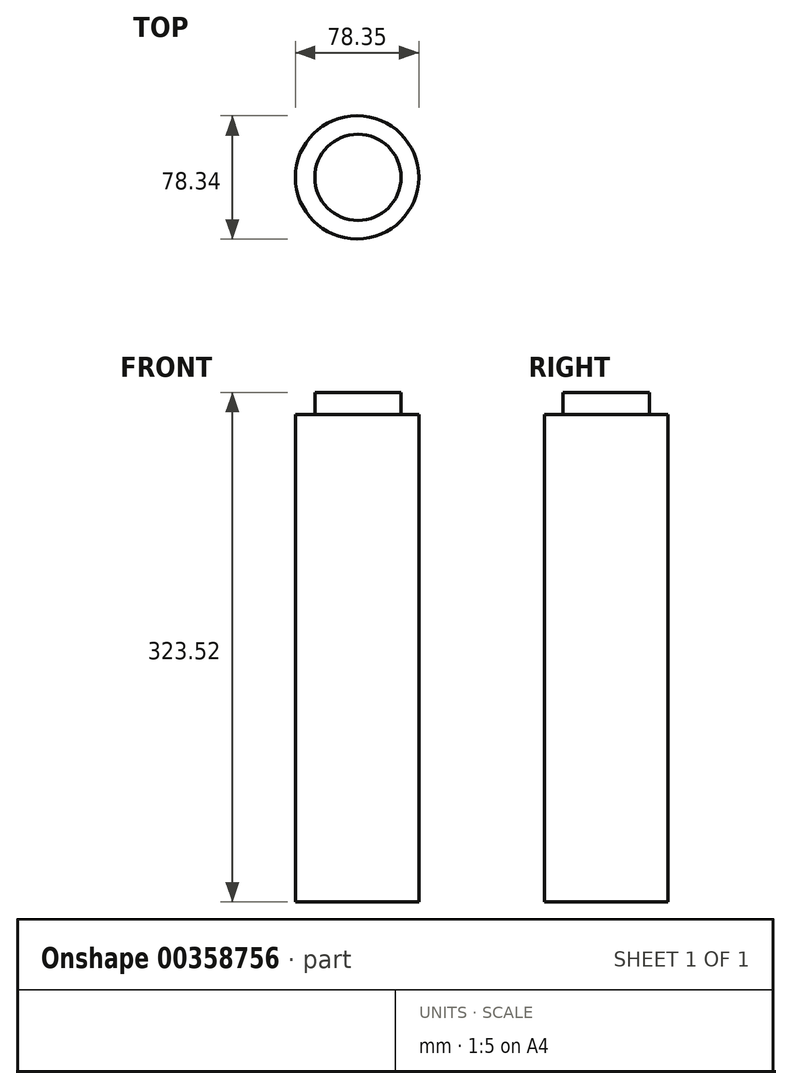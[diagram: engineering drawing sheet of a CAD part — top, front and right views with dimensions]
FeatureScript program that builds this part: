
annotation { "Feature Type Name" : "Feature", "Feature Type Description" : "" }
export const myFeature = defineFeature(function(context is Context, id is Id, definition is map)
    precondition{}
    {
        {
            var Q0;
            Q0=qCreatedBy(makeId("Top.planeOp"),FACE);
            var sketch = newSketch(context, id + "F0", { "sketchPlane" : qUnion([Q0])});
            skCircle(sketch, "E0", {"center": v(-1.87, 0) * mm, "radius": 39.17 * mm});
            skSolve(sketch);
        }
        {
            var Q0;
            Q0 = qSketchRegion(id + "F0", true);
            extrude(context, id + "F1", {"entities" : qUnion([Q0]), "depth" : 309.5 * mm});
        }
        {
            var Q0;
            Q0=makeQuery(id+"F1.opExtrude","SWEPT_BODY",BODY,{"disambiguationData":[OSD([sQuery(id+"F0.wireOp",EDGE,"E0")])]});
            transform(context, id + "F2", {"entities" : qUnion([Q0]), "transformType" : TransformType.TRANSLATION_3D, "dx" : 0 * mm, "dy" : 0 * mm, "dz" : 25 * mm, "makeCopy" : true});
        }
        {
            var Q0;
            Q0=makeQuery(id+"F2.opPattern","COPY",BODY,{"derivedFrom":makeQuery(id+"F1.opExtrude","SWEPT_BODY",BODY,{"disambiguationData":[OSD([sQuery(id+"F0.wireOp",EDGE,"E0")])]}),"instanceName":"1"});
            var Q1;
            Q1=sQuery(id+"F0.wireOp",VERTEX,"E0.center");
            transform(context, id + "F3", {"entities" : qUnion([Q0]), "transformType" : TransformType.SCALE_UNIFORMLY, "scale" : .7, "scalePoint" : qUnion([Q1]), "makeCopy" : false});
        }
        {
            var Q0;
            Q0=makeQuery(id+"F2.opPattern","COPY",BODY,{"derivedFrom":makeQuery(id+"F1.opExtrude","SWEPT_BODY",BODY,{"disambiguationData":[OSD([sQuery(id+"F0.wireOp",EDGE,"E0")])]}),"instanceName":"1"});
            deleteBodies(context, id + "F4", {"entities" : qUnion([Q0])});
        }
        {
            var Q0;
            Q0=makeQuery(id+"F1.opExtrude","SWEPT_BODY",BODY,{"disambiguationData":[OSD([sQuery(id+"F0.wireOp",EDGE,"E0")])]});
            transform(context, id + "F5", {"entities" : qUnion([Q0]), "transformType" : TransformType.TRANSLATION_3D, "dx" : 0 * mm, "dy" : 0 * mm, "dz" : 14.1 * mm, "makeCopy" : true});
        }
        {
            var Q0;
            Q0=makeQuery(id+"F5.opPattern","COPY",BODY,{"derivedFrom":makeQuery(id+"F1.opExtrude","SWEPT_BODY",BODY,{"disambiguationData":[OSD([sQuery(id+"F0.wireOp",EDGE,"E0")])]}),"instanceName":"1"});
            var Q1;
            Q1=qCreatedBy(makeId("Origin.pointOp"),VERTEX);
            transform(context, id + "F6", {"entities" : qUnion([Q0]), "transformType" : TransformType.SCALE_UNIFORMLY, "scale" : .7, "scalePoint" : qUnion([Q1]), "makeCopy" : false});
        }
        {
            var Q0;
            Q0=makeQuery(id+"F5.opPattern","COPY",FACE,{"derivedFrom":makeQuery(id+"F1.opExtrude","CAP_FACE",FACE,{"disambiguationData":[OSD([sQuery(id+"F0.wireOp",EDGE,"E0")])],"isStart":false}),"instanceName":"1"});
            extrude(context, id + "F7", {"entities" : qUnion([Q0]), "operationType" : NewBodyOperationType.ADD, "depth" : 97 * mm});
        }
    });
